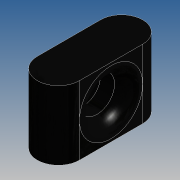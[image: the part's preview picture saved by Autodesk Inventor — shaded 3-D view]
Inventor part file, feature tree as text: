
AUTODESK INVENTOR PART (.ipt)
format: ipt  version: 2015 SP1 (Build 190203100, 203)  size: 247,808 bytes
history: native  units: mm
features: fillet x2, sketch x2, extrude x1, mirror x1, hole x1
ambient origin geometry x8: Origin, YZ Plane, XZ Plane, XY Plane, X Axis, Y Axis, Z Axis, Center Point
bodies: Solid1 (feature_tree)
feature tree (7):
  extrude  "Extrusion1"  Depth=9.8mm
  fillet  "Fillet1"  Radius=9.8mm
  mirror  "Mirror1"
  hole  "Hole1"  [1 undecoded]
  fillet  "Fillet2"  [1 undecoded]
  sketch  "Sketch1"  dims[d0=6.0mm d1=7.5mm d2=9.8mm d3=0.0mm]
  sketch  "Sketch2"  dims[d4=3.0mm d5=5.0mm d6=6.0mm d7=4.0mm d8=2.0mm d9=90.0deg d10=8.0mm d11=20.594885mm d12=2.0mm]
note: 2 required parameter values undecoded (feature->parameter linkage not recoverable at this tier; creation-order binding heuristic only, values carry confidence <= 0.55)
